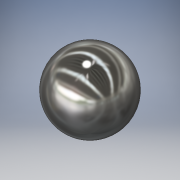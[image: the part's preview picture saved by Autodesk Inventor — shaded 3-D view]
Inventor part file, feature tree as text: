
AUTODESK INVENTOR PART (.ipt)
format: ipt  version: 2016 (Build 200138000, 138)  size: 144,896 bytes
history: native  units: in
note: dims shown in document units (in); Inventor stores cm internally (conversion verified against a paired STEP export)
features: revolve x1, sketch x1
ambient origin geometry x8: Origin, YZ Plane, XZ Plane, XY Plane, X Axis, Y Axis, Z Axis, Center Point
bodies: Solid1 (feature_tree)
feature tree (2):
  revolve  "Revolution1"  Angle=90.0deg
  sketch  "Sketch1"  dims[d0=0.687in d1=90.0deg]
